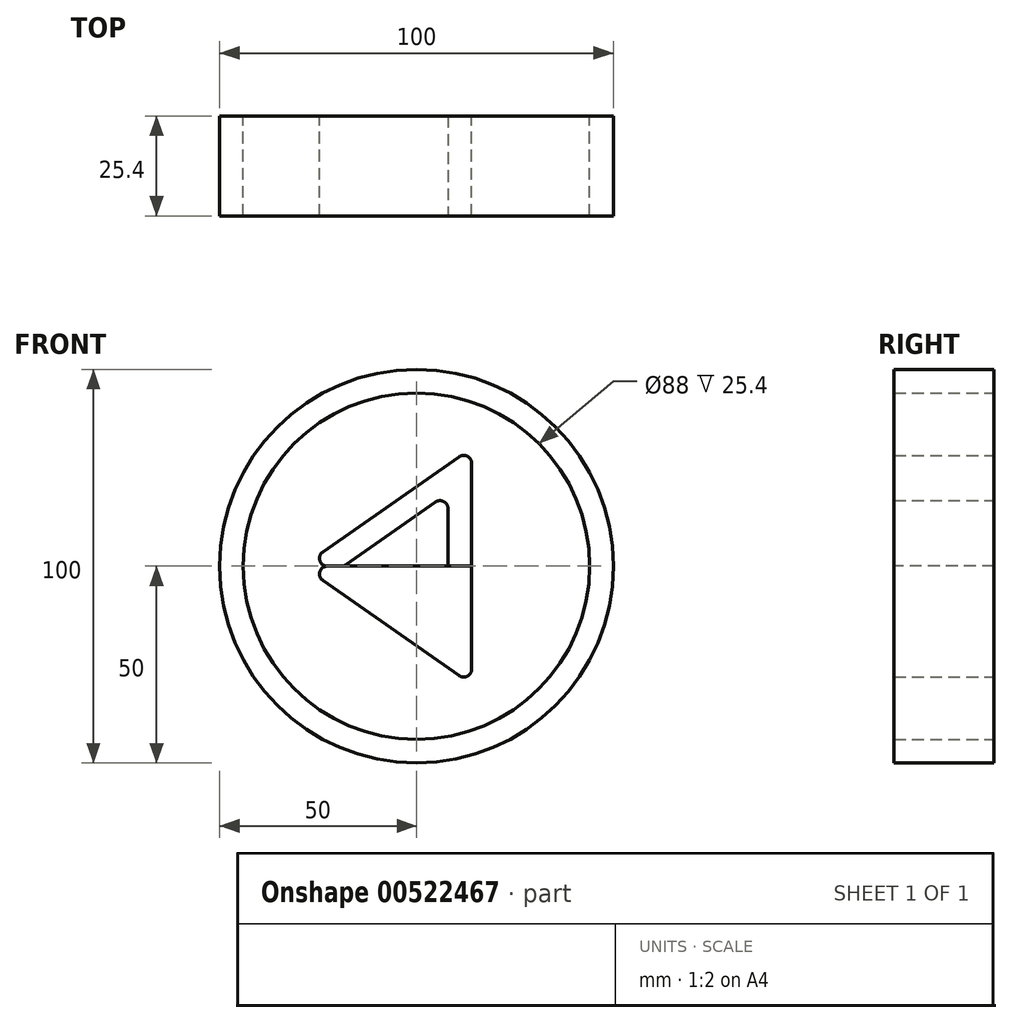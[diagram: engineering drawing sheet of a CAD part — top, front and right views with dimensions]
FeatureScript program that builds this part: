
annotation { "Feature Type Name" : "Feature", "Feature Type Description" : "" }
export const myFeature = defineFeature(function(context is Context, id is Id, definition is map)
    precondition{}
    {
        {
            var Q0;
            Q0=qCreatedBy(makeId("Front.planeOp"),FACE);
            var sketch = newSketch(context, id + "F0", { "sketchPlane" : qUnion([Q0])});
            skCircle(sketch, "E0", {"center": v(0, 0) * mm, "radius": 50 * mm});
            skCircle(sketch, "E1", {"center": v(0, 0) * mm, "radius": 44 * mm});
            skPoint(sketch, "E2", {"position": v(0, -50) * mm});
            skLineSegment(sketch, "E3", {"start": v(0, 0) * mm, "end": v(-29, 0) * mm});
            skLineSegment(sketch, "E4", {"start": v(-29, 0) * mm, "end": v(14, 30) * mm});
            skLineSegment(sketch, "E5", {"start": v(14, 30) * mm, "end": v(14, 0) * mm});
            skLineSegment(sketch, "E6", {"start": v(14, 0) * mm, "end": v(0, 0) * mm});
            skSolve(sketch);
        }
        {
            var Q0;
            Q0=makeQuery(id+"F0.imprint","IMPRINT",FACE,{"disambiguationData":[TD([[makeQuery(id+"F0.imprint","IMPRINT",EDGE,{"derivedFrom":sQuery(id+"F0.wireOp",EDGE,"E0")}),1.0]])]});
            var Q1;
            {var subQ9=sQuery(id+"F0.wireOp",EDGE,"JPuuaeZV-5oA1-bOET-emPB-8E9oC848Bjk7");Q1=makeQuery(id+"F0.imprint","IMPRINT",FACE,{"disambiguationData":[TD([[makeQuery(id+"F0.imprint","IMPRINT",EDGE,{"derivedFrom":subQ9}),1.0]])]});}
            var Q2;
            {var subQ1=sQuery(id+"F0.wireOp",EDGE,"1czAJEjm-GAaO-qJbW-bNPJ-VOC9MhbBWLXS");var subQ3=sQuery(id+"F0.wireOp",EDGE,"90a05c53-9c47-40ab-b859-f5c182912d02.1");var subQ4=makeQuery(id+"F0.imprint","INTERSECT",VERTEX,{"derivedFrom":[subQ1,subQ3]});Q2=makeQuery(id+"F0.imprint","IMPRINT",FACE,{"disambiguationData":[TD([[makeQuery(id+"F0.imprint","IMPRINT",EDGE,{"disambiguationData":[TD([[subQ4,-1.0]])],"derivedFrom":subQ3}),1.0]])]});}
            extrude(context, id + "F1", {"entities" : qUnion([Q0, Q1, Q2]), "depth" : 25.4 * mm});
        }
        {
            var Q0;
            Q0=makeQuery(id+"F0.imprint","IMPRINT",FACE,{"disambiguationData":[TD([[makeQuery(id+"F0.imprint","IMPRINT",EDGE,{"derivedFrom":sQuery(id+"F0.wireOp",EDGE,"E3")}),-1.0]])]});
            extrude(context, id + "F2", {"entities" : qUnion([Q0]), "depth" : 25.4 * mm, "offsetDistance" : 25.4 * mm});
        }
        {
            var Q0;
            Q0=makeQuery(id+"F2.opExtrude","SWEPT_BODY",BODY,{"disambiguationData":[OSD([sQuery(id+"F0.wireOp",EDGE,"E3"),sQuery(id+"F0.wireOp",EDGE,"E4"),sQuery(id+"F0.wireOp",EDGE,"E5"),sQuery(id+"F0.wireOp",EDGE,"E6")])]});
            var Q1;
            Q1=makeQuery(id+"F2.opExtrude","SWEPT_FACE",FACE,{"disambiguationData":[OSD([sQuery(id+"F0.wireOp",EDGE,"E3"),sQuery(id+"F0.wireOp",EDGE,"E6")])]});
            mirror(context, id + "F3", {"operationType" : NewBodyOperationType.ADD, "entities" : qUnion([Q0]), "mirrorPlane" : qUnion([Q1])});
        }
        {
            var Q0;
            {var subQ0=makeQuery(id+"F2.opExtrude","CAP_FACE",FACE,{"disambiguationData":[OSD([sQuery(id+"F0.wireOp",EDGE,"E3"),sQuery(id+"F0.wireOp",EDGE,"E4"),sQuery(id+"F0.wireOp",EDGE,"E5"),sQuery(id+"F0.wireOp",EDGE,"E6")])],"isStart":false});Q0=makeQuery(id+"F3.boolean.opBoolean","MERGE",FACE,{"derivedFrom":[subQ0,makeQuery(id+"F3.opPattern","COPY",FACE,{"derivedFrom":subQ0,"instanceName":"1"})]});}
            var sketch = newSketch(context, id + "F4", { "sketchPlane" : qUnion([Q0])});
            skLineSegment(sketch, "E7.0", {"start": v(8, 18.5) * mm, "end": v(-18.51, 0) * mm});
            skLineSegment(sketch, "E7.1", {"start": v(8, -18.5) * mm, "end": v(8, 18.5) * mm});
            skLineSegment(sketch, "E7.2", {"start": v(-18.51, 0) * mm, "end": v(8, -18.5) * mm});
            skSolve(sketch);
        }
        {
            var Q0;
            Q0=makeQuery(id+"F4.imprint","IMPRINT",FACE,{"disambiguationData":[TD([[makeQuery(id+"F4.imprint","IMPRINT",EDGE,{"derivedFrom":sQuery(id+"F4.wireOp",EDGE,"E7.0")}),1.0]])]});
            extrude(context, id + "F5", {"entities" : qUnion([Q0]), "operationType" : NewBodyOperationType.REMOVE, "oppositeDirection" : true, "depth" : 25.4 * mm, "offsetDistance" : 25.4 * mm});
        }
        {
            var Q0;
            Q0=makeQuery(id+"F3.opPattern","COPY",EDGE,{"derivedFrom":makeQuery(id+"F2.opExtrude","SWEPT_EDGE",EDGE,{"disambiguationData":[OSD([sQuery(id+"F0.wireOp",EDGE,"E4"),sQuery(id+"F0.wireOp",EDGE,"E5")])]}),"instanceName":"1"});
            var Q1;
            {var subQ0=makeQuery(id+"F2.opExtrude","SWEPT_EDGE",EDGE,{"disambiguationData":[OSD([sQuery(id+"F0.wireOp",EDGE,"E3"),sQuery(id+"F0.wireOp",EDGE,"E4")])]});Q1=makeQuery(id+"F3.boolean.opBoolean","MERGE",EDGE,{"derivedFrom":[subQ0,makeQuery(id+"F3.opPattern","COPY",EDGE,{"derivedFrom":subQ0,"instanceName":"1"})]});}
            var Q2;
            Q2=makeQuery(id+"F2.opExtrude","SWEPT_EDGE",EDGE,{"disambiguationData":[OSD([sQuery(id+"F0.wireOp",EDGE,"E4"),sQuery(id+"F0.wireOp",EDGE,"E5")])]});
            var Q3;
            Q3=makeQuery(id+"F5.boolean.opBoolean","COPY",EDGE,{"derivedFrom":makeQuery(id+"F5.opExtrude","SWEPT_EDGE",EDGE,{"disambiguationData":[OSD([sQuery(id+"F4.wireOp",EDGE,"E7.0"),sQuery(id+"F4.wireOp",EDGE,"E7.1")])]})});
            var Q4;
            Q4=makeQuery(id+"F5.boolean.opBoolean","COPY",EDGE,{"derivedFrom":makeQuery(id+"F5.opExtrude","SWEPT_EDGE",EDGE,{"disambiguationData":[OSD([sQuery(id+"F4.wireOp",EDGE,"E7.0"),sQuery(id+"F4.wireOp",EDGE,"E7.2")])]})});
            var Q5;
            Q5=makeQuery(id+"F5.boolean.opBoolean","COPY",EDGE,{"derivedFrom":makeQuery(id+"F5.opExtrude","SWEPT_EDGE",EDGE,{"disambiguationData":[OSD([sQuery(id+"F4.wireOp",EDGE,"E7.1"),sQuery(id+"F4.wireOp",EDGE,"E7.2")])]})});
            fillet(context, id + "F6", {"entities" : qUnion([Q0, Q1, Q2, Q3, Q4, Q5]), "radius" : 2 * mm, "tangentPropagation" : true, "allowEdgeOverflow" : false});
        }
    });
